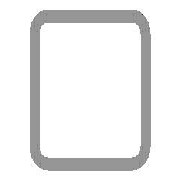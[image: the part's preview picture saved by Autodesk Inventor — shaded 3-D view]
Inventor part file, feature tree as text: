
AUTODESK INVENTOR PART (.ipt)
format: ipt  version: 2025 (Build 290162010, 162A)  size: 134,656 bytes
history: native  units: mm (DEFAULTED — no unit token found)
features: other x4, sketch x1, plane x1
ambient origin geometry x8: Origin, YZ Plane, XZ Plane, XY Plane, X Axis, Y Axis, Z Axis, Center Point
bodies: Solid1 (feature_tree), Body (feature_tree)
feature tree (6):
  parser-record x1  (decoder bookkeeping rows leaked as tree rows — omitted from the tree; the rows remain in map.json)
  other  "Driven Length"
  other  "Start Plane"
  other  "End Plane"
  sketch  "Sketch3"  dims[d3=1170.0mm d4=0.0mm d7=4.0mm d9=40.0mm d11=40.0mm d12=2.0mm d13=40.0mm d14=1210.0mm d15=20.0mm d16=20.0mm d17=90.0deg d18=1170.0mm]
  plane  "Work Plane3"
